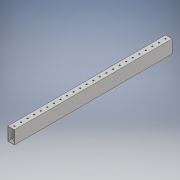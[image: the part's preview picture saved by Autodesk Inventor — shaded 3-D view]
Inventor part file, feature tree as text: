
AUTODESK INVENTOR PART (.ipt)
format: ipt  version: 2018 (Build 220112000, 112)  size: 222,208 bytes
history: native  units: in
note: dims shown in document units (in); Inventor stores cm internally (conversion verified against a paired STEP export)
features: extrude x3, sketch x3
ambient origin geometry x8: Origin, YZ Plane, XZ Plane, XY Plane, X Axis, Y Axis, Z Axis, Center Point
bodies: Solid1 (feature_tree)
feature tree (6):
  extrude  "Extrusion1"  Depth=2.0in
  extrude  "Extrusion2"  Depth=0.0625in TaperAngle=0.0deg
  extrude  "Extrusion3"  Depth=1.0in
  sketch  "Sketch1"  dims[d0=1.0in d1=2.0in]
  sketch  "Sketch2"  dims[d2=0.0625in d3=27.0in d4=0.0in]
  sketch  "Sketch3"  dims[d5=0.5in d6=1.0in d7=1.0in d8=1.0in d9=1.0in d10=1.0in d11=1.0in d12=1.0in d13=1.0in d14=1.0in d15=1.0in d16=1.0in d17=1.0in d18=1.0in d19=1.0in d20=1.0in d21=1.0in d22=1.0in d23=1.0in d24=1.0in d25=1.0in d26=1.0in d27=1.0in d28=1.0in d29=1.0in d30=1.0in d31=1.0in d32=1.0in d33=1.0in d34=0.203in d35=0.203in d36=0.203in d37=0.203in d38=0.203in d39=0.203in d40=0.203in d41=0.203in d42=0.203in d43=0.203in d44=0.203in d45=0.203in d46=0.203in d47=0.203in d48=0.203in d49=0.203in d50=0.203in d51=0.203in d52=0.203in d53=0.203in d54=0.203in d55=0.203in d56=0.203in d57=0.203in d58=0.203in d59=0.203in d60=0.203in d61=27.0in d62=0.0in d63=2.75in d64=2.0in d65=1.0in d66=2.0in d67=0.0in]
